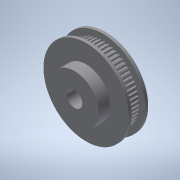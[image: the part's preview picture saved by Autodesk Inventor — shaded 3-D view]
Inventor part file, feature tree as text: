
AUTODESK INVENTOR PART (.ipt)
format: ipt  version: 2022 (Build 260153000, 153)  size: 261,120 bytes
history: native  units: mm
features: sketch x2, revolve x1, extrude x1, pattern_circular x1
ambient origin geometry x8: Origin, YZ Plane, XZ Plane, XY Plane, X Axis, Y Axis, Z Axis, Center Point
bodies: Solid1 (feature_tree)
feature tree (5):
  revolve  "Revolution1"  [1 undecoded]
  extrude  "Extrusion1"  Depth=18.95mm
  pattern_circular  "Circular Pattern1"  Angle=90.0deg  [1 undecoded]
  sketch  "Sketch1"  dims[d0=4.0mm d1=7.0mm]
  sketch  "Sketch2"  dims[d4=1.5mm d6=18.95mm d7=90.0deg d8=1.3mm d9=18.85mm d10=10.0mm d11=0.0mm d12=600.0mm d13=360.0deg d15=22.0mm d16=6.0mm d17=12.5mm]
note: 2 required parameter values undecoded (feature->parameter linkage not recoverable at this tier; creation-order binding heuristic only, values carry confidence <= 0.55)